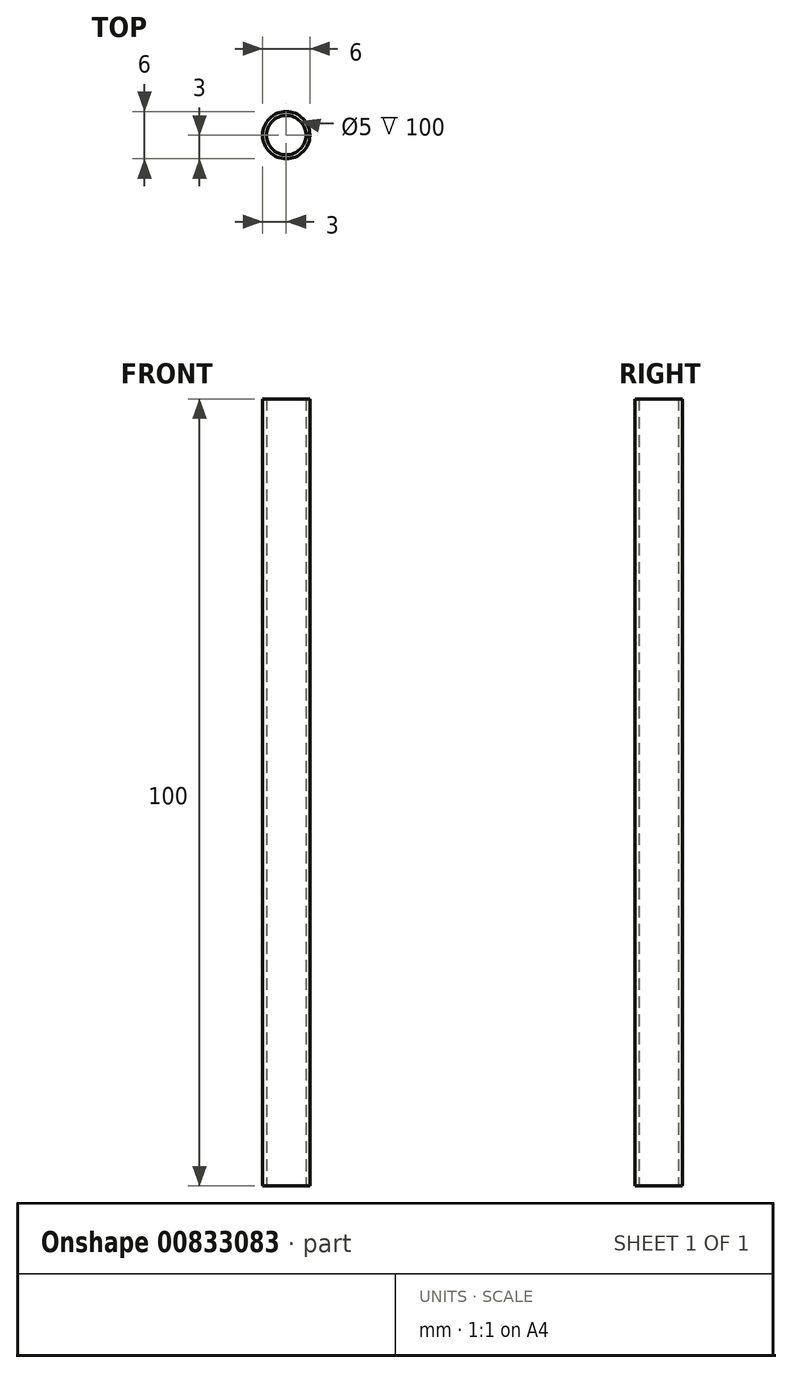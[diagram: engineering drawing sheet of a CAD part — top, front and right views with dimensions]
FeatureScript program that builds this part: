
annotation { "Feature Type Name" : "Feature", "Feature Type Description" : "" }
export const myFeature = defineFeature(function(context is Context, id is Id, definition is map)
    precondition{}
    {
        {
            var Q0;
            Q0=qCreatedBy(makeId("Top.planeOp"),FACE);
            var sketch = newSketch(context, id + "F0", { "sketchPlane" : qUnion([Q0])});
            skCircle(sketch, "E0", {"center": v(0, 0) * mm, "radius": 3 * mm});
            skCircle(sketch, "E1", {"center": v(0, 0) * mm, "radius": 2.5 * mm});
            skSolve(sketch);
        }
        {
            var Q0;
            Q0 = qSketchRegion(id + "F0", true);
            extrude(context, id + "F1", {"entities" : qUnion([Q0]), "depth" : 100 * mm, "offsetDistance" : 25 * mm});
        }
    });
